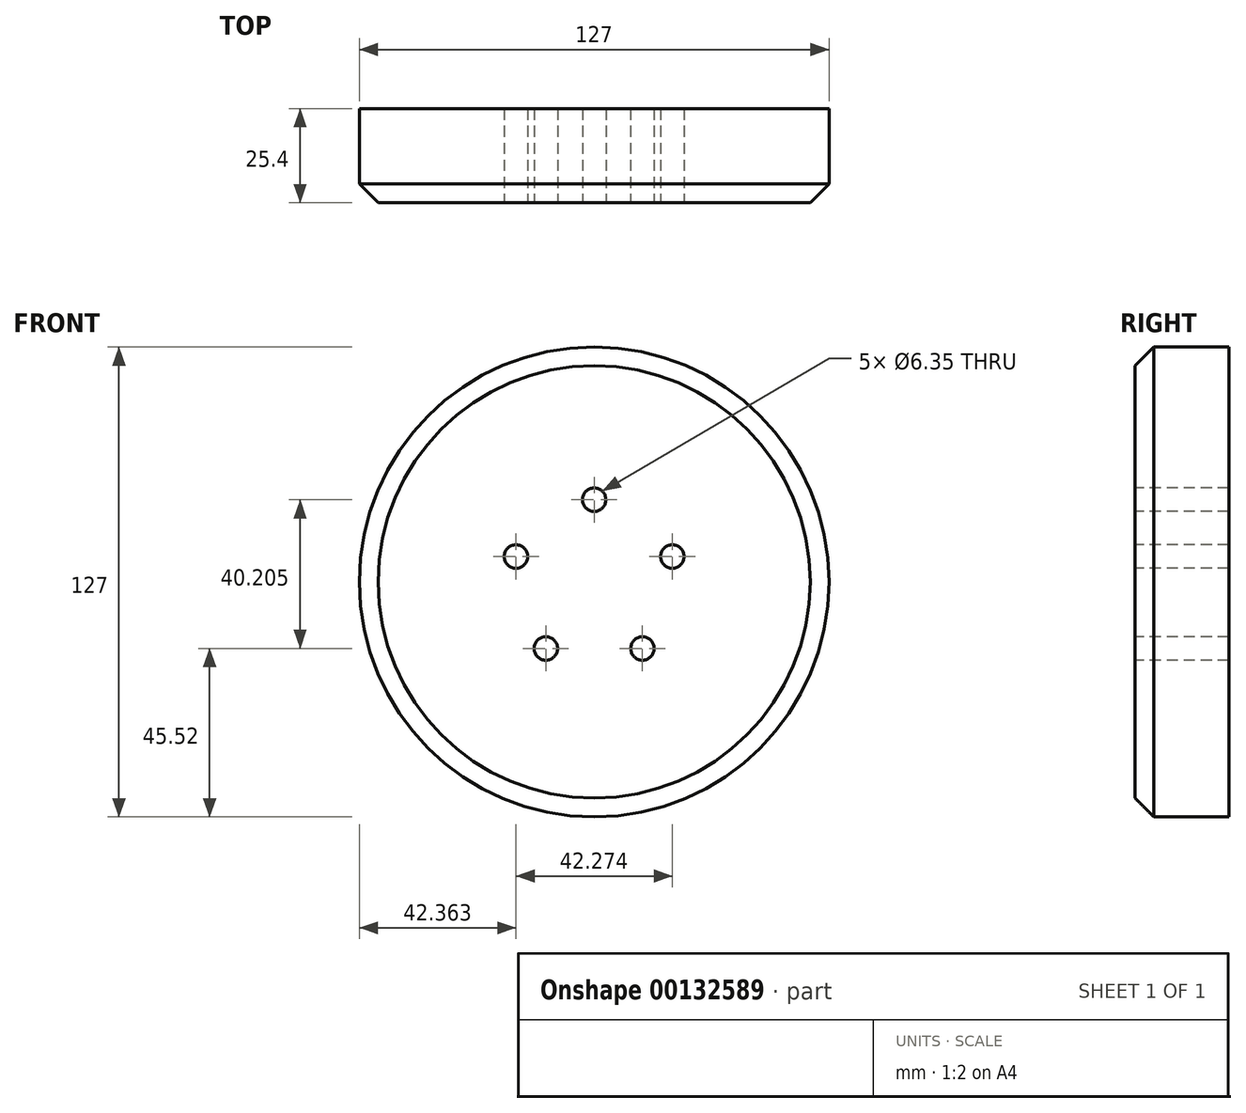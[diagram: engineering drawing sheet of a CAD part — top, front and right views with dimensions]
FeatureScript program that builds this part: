
annotation { "Feature Type Name" : "Feature", "Feature Type Description" : "" }
export const myFeature = defineFeature(function(context is Context, id is Id, definition is map)
    precondition{}
    {
        {
            var Q0;
            Q0=qCreatedBy(makeId("Front.planeOp"),FACE);
            var sketch = newSketch(context, id + "F0", { "sketchPlane" : qUnion([Q0])});
            skCircle(sketch, "E0", {"center": v(0, 0) * mm, "radius": 63.5 * mm});
            skSolve(sketch);
        }
        {
            var Q0;
            Q0=makeQuery(id+"F0.imprint","IMPRINT",FACE,{"disambiguationData":[TD([[makeQuery(id+"F0.imprint","IMPRINT",EDGE,{"derivedFrom":sQuery(id+"F0.wireOp",EDGE,"E0")}),1.0]])]});
            extrude(context, id + "F1", {"entities" : qUnion([Q0]), "endBound" : BoundingType.SYMMETRIC, "depth" : 25.4 * mm});
        }
        {
            var Q0;
            Q0=makeQuery(id+"F1.opExtrude","CAP_FACE",FACE,{"disambiguationData":[OSD([sQuery(id+"F0.wireOp",EDGE,"E0")])],"isStart":false});
            var sketch = newSketch(context, id + "F2", { "sketchPlane" : qUnion([Q0])});
            skCircle(sketch, "E1", {"center": v(0, 22.23) * mm, "radius": 3.18 * mm});
            skCircle(sketch, "E2.1.0", {"center": v(-21.14, 6.87) * mm, "radius": 3.18 * mm});
            skCircle(sketch, "E2.2.0", {"center": v(-13.06, -17.98) * mm, "radius": 3.18 * mm});
            skCircle(sketch, "E2.3.0", {"center": v(13.06, -17.98) * mm, "radius": 3.18 * mm});
            skCircle(sketch, "E2.4.0", {"center": v(21.14, 6.87) * mm, "radius": 3.18 * mm});
            skPoint(sketch, "E2.center", {"position": v(0, 0) * mm});
            skSolve(sketch);
        }
        {
            var Q0;
            Q0=sQuery(id+"F2.wireOp",VERTEX,"E1.center");
            var Q1;
            Q1=sQuery(id+"F2.wireOp",VERTEX,"E2.4.0.center");
            var Q2;
            Q2=sQuery(id+"F2.wireOp",VERTEX,"E2.3.0.center");
            var Q3;
            Q3=sQuery(id+"F2.wireOp",VERTEX,"E2.2.0.center");
            var Q4;
            Q4=sQuery(id+"F2.wireOp",VERTEX,"E2.1.0.center");
            var Q5;
            Q5=makeQuery(id+"F1.opExtrude","SWEPT_BODY",BODY,{"disambiguationData":[OSD([sQuery(id+"F0.wireOp",EDGE,"E0")])]});
            hole(context, id + "F3", {"style" : HoleStyle.SIMPLE, "endStyle" : HoleEndStyle.THROUGH, "holeDiameter" : 6.35 * mm, "locations" : qUnion([Q0, Q1, Q2, Q3, Q4]), "scope" : qUnion([Q5]), "isTappedThrough" : true});
        }
        {
            var Q0;
            Q0=makeQuery(id+"F1.opExtrude","CAP_EDGE",EDGE,{"disambiguationData":[OSD([sQuery(id+"F0.wireOp",EDGE,"E0")])],"isStart":false});
            chamfer(context, id + "F4", {"entities" : qUnion([Q0]), "width" : 5.08 * mm, "tangentPropagation" : true});
        }
    });
